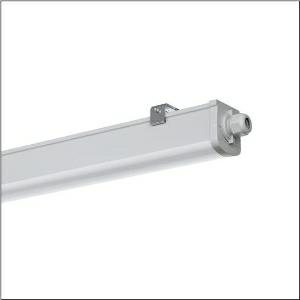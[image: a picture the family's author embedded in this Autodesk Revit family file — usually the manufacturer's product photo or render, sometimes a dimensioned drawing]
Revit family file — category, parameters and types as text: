
# Revit family: monsun_r__31_51fa20dp430b_5f21
name_source: partatom
category: Lighting Fixtures
units: mm (PartAtom-declared; Revit-internal decimal feet)

## family parameters
Cut with Voids When Loaded = No
Host = Face
Light Source = No
Part Type = Normal
Room Calculation Point = No
Round Connector Dimension = Use Diameter
Shared = No

## types (1)
- Monsun® 31 (1 x LED, 3800 lm, 28 W, 4000K)
    Apparent Load = 28 VA
    CIE Flux Codes = 42 72 91 92 100
    Color Rendering = 80
    Color Temperature = 4000K
    Default Elevation = 1800 mm
    Description = Monsun® 31, damp-proof luminaire, primary optical cover: diffuser, of PC, frosted, light emission: direct distribution, primary light characteristic: symmetric, installation type: surface-mounted, LED, rated luminous flux: 3.800lm, luminous efficacy: 136lm/W, light colour: 840, colour temperature: 4000K, control gear: ECG, with terminal, 5+1-pole, max. 2.5mm², through-wiring: 3x 2.5mm² + 3x 1.5mm², mains connection: 220..240V, AC, 50/60Hz, rated input power: 28W, housing, luminaire housing, of PC, light grey (RAL 7035), length: 1.458mm, width: 68mm, height: 76mm, protection rating (complete): IP66, insulation class (complete): insulation class II (safety insulation), certification: CE, ENEC, UKCA, protection symbol: D, impact resistance: IK08, permissible operating ambient temperature: -20..+40°C, corresponds to IFS (International Featured Standards) requirements for safety and quality in the food industry, packaging unit: 1 piece
    Height = 77 mm
    Lamp = 1 x LED
    Lamp Light Flux = 3800 lm
    Lamp Power = 28 W
    Lamp count = 1
    Length = 1518 mm
    Luminous efficacy = 136 lm/W
    Manufacturer = Siteco
    ModVariant = No
    Model = 51FA20DP430B
    Mounting Place = Ceiling
    Mounting Type = Surface mounted
    Number of Poles = 1
    OnlyDefault = Yes
    Power Factor = 1
    Product Name = Monsun® 31
    Product group = damp-proof luminaire | ceiling mounted
    ProductGroupID = 300
    Protection Class = Protection class II
    Protection Degree = IP 66
    RLX_Detail_Level = 1
    RlxData = <blob elided: 32917 chars, md5=61dd1f3a>
    Socket = socket
    Standby Power = 0 W
    System Light Flux = 3800 lm
    System Power = 28 W
    Type Comments = Product without accessories
    Type Image = l_1006174.jpg
    URL = http://relux.com
    VarID = ---
    Voltage = 0 V
    Weight = 0.00 kg
    Width = 69 mm

## geometry (parser evidence)
native form markers: Blend x4, Sweep x12
no freeform markers — native parametric forms only
